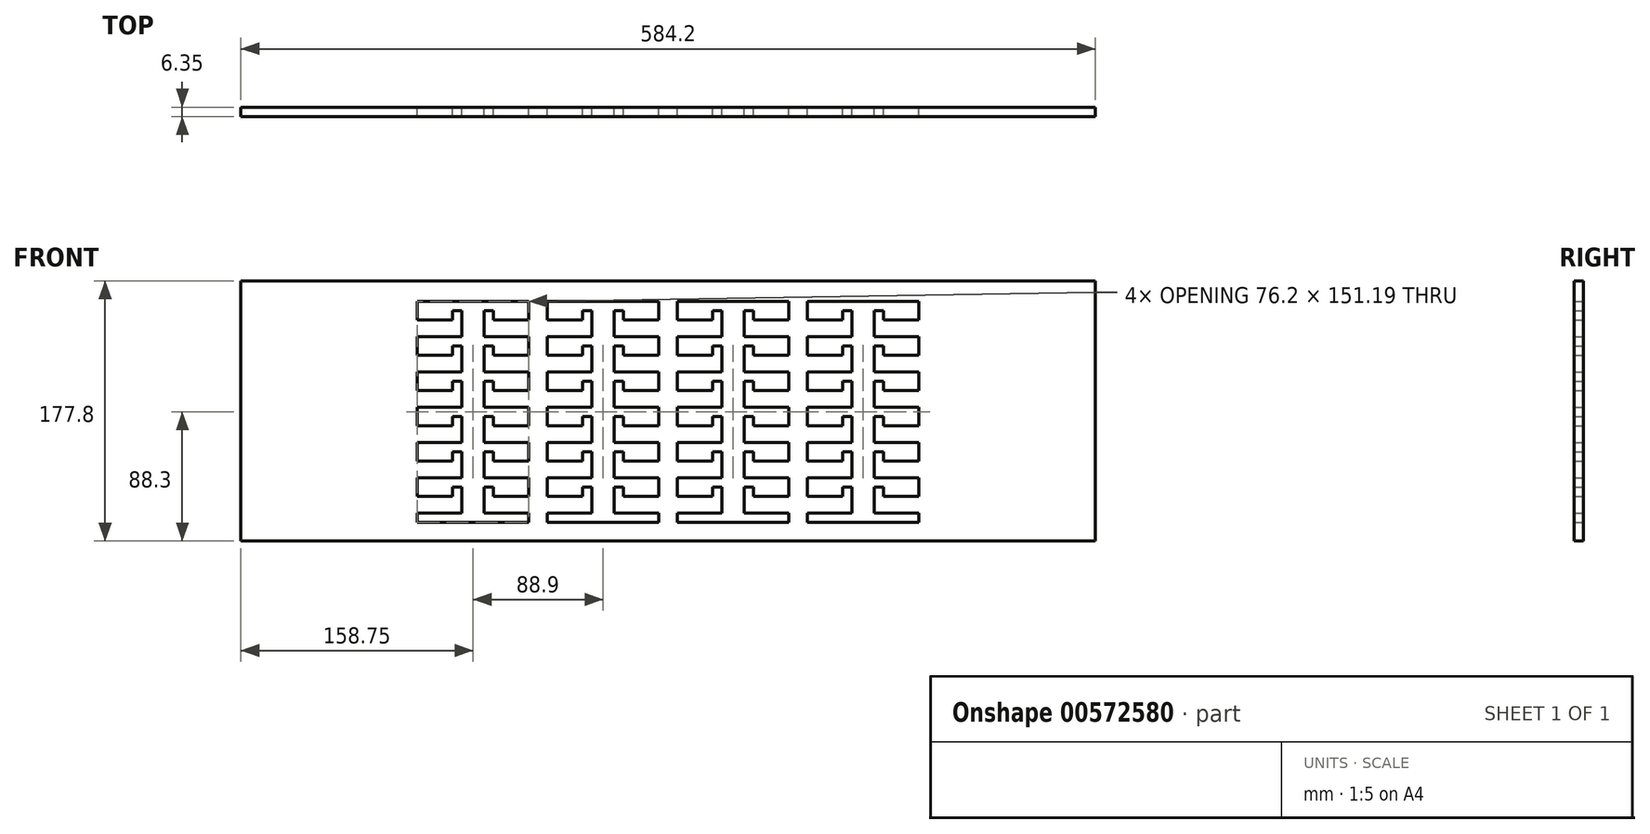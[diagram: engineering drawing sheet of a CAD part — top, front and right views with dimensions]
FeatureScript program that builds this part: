
annotation { "Feature Type Name" : "Feature", "Feature Type Description" : "" }
export const myFeature = defineFeature(function(context is Context, id is Id, definition is map)
    precondition{}
    {
        {
            var Q0;
            Q0=qCreatedBy(makeId("Front.planeOp"),FACE);
            var sketch = newSketch(context, id + "F0", { "sketchPlane" : qUnion([Q0])});
            skLineSegment(sketch, "E0", {"start": v(-97.96, -49.5) * mm, "end": v(-67.48, -49.5) * mm});
            skLineSegment(sketch, "E1", {"start": v(-67.48, -49.5) * mm, "end": v(-67.48, -31.72) * mm});
            skLineSegment(sketch, "E2", {"start": v(-67.48, -31.72) * mm, "end": v(-73.83, -31.72) * mm});
            skLineSegment(sketch, "E3", {"start": v(-73.83, -31.72) * mm, "end": v(-73.83, -38.07) * mm});
            skLineSegment(sketch, "E4", {"start": v(-73.83, -38.07) * mm, "end": v(-97.96, -38.07) * mm});
            skLineSegment(sketch, "E5", {"start": v(-97.96, -38.07) * mm, "end": v(-97.96, -25.37) * mm});
            skLineSegment(sketch, "E6", {"start": v(-97.96, -25.37) * mm, "end": v(-67.48, -25.37) * mm});
            skLineSegment(sketch, "E7", {"start": v(-67.48, -25.37) * mm, "end": v(-67.48, -7.6) * mm});
            skLineSegment(sketch, "E8", {"start": v(-67.48, -7.6) * mm, "end": v(-73.83, -7.6) * mm});
            skLineSegment(sketch, "E9", {"start": v(-73.83, -7.6) * mm, "end": v(-73.83, -13.94) * mm});
            skLineSegment(sketch, "E10", {"start": v(-73.83, -13.94) * mm, "end": v(-97.96, -13.94) * mm});
            skLineSegment(sketch, "E11", {"start": v(-97.96, -13.94) * mm, "end": v(-97.96, -1.24) * mm});
            skLineSegment(sketch, "E12", {"start": v(-97.96, -1.24) * mm, "end": v(-67.48, -1.24) * mm});
            skLineSegment(sketch, "E13", {"start": v(-67.48, -1.24) * mm, "end": v(-67.48, 16.54) * mm});
            skLineSegment(sketch, "E14", {"start": v(-67.48, 16.54) * mm, "end": v(-73.83, 16.54) * mm});
            skLineSegment(sketch, "E15", {"start": v(-73.83, 16.54) * mm, "end": v(-73.83, 10.19) * mm});
            skLineSegment(sketch, "E16", {"start": v(-73.83, 10.19) * mm, "end": v(-97.96, 10.19) * mm});
            skLineSegment(sketch, "E17", {"start": v(-97.96, 10.19) * mm, "end": v(-97.96, 22.89) * mm});
            skLineSegment(sketch, "E18", {"start": v(-97.96, 22.89) * mm, "end": v(-67.48, 22.89) * mm});
            skLineSegment(sketch, "E19", {"start": v(-67.48, 22.89) * mm, "end": v(-67.48, 40.67) * mm});
            skLineSegment(sketch, "E20", {"start": v(-67.48, 40.67) * mm, "end": v(-73.83, 40.67) * mm});
            skLineSegment(sketch, "E21", {"start": v(-73.83, 40.67) * mm, "end": v(-73.83, 34.32) * mm});
            skLineSegment(sketch, "E22", {"start": v(-73.83, 34.32) * mm, "end": v(-97.96, 34.32) * mm});
            skLineSegment(sketch, "E23", {"start": v(-97.96, 34.32) * mm, "end": v(-97.96, 47.02) * mm});
            skLineSegment(sketch, "E24", {"start": v(-97.96, 47.02) * mm, "end": v(-67.48, 47.02) * mm});
            skLineSegment(sketch, "E25", {"start": v(-67.48, 64.8) * mm, "end": v(-73.83, 64.8) * mm});
            skLineSegment(sketch, "E26", {"start": v(-73.83, 64.8) * mm, "end": v(-73.83, 58.45) * mm});
            skLineSegment(sketch, "E27", {"start": v(-73.83, 58.45) * mm, "end": v(-97.96, 58.45) * mm});
            skLineSegment(sketch, "E28", {"start": v(-97.96, 58.45) * mm, "end": v(-97.96, 71.15) * mm});
            skLineSegment(sketch, "E29", {"start": v(-21.76, -80.05) * mm, "end": v(-21.76, -73.63) * mm});
            skLineSegment(sketch, "E30", {"start": v(-21.76, -73.63) * mm, "end": v(-52.24, -73.63) * mm});
            skLineSegment(sketch, "E31", {"start": v(-52.24, -73.63) * mm, "end": v(-52.24, -55.85) * mm});
            skLineSegment(sketch, "E32", {"start": v(-52.24, -55.85) * mm, "end": v(-45.89, -55.85) * mm});
            skLineSegment(sketch, "E33", {"start": v(-45.89, -55.85) * mm, "end": v(-45.89, -62.2) * mm});
            skLineSegment(sketch, "E34", {"start": v(-45.89, -62.2) * mm, "end": v(-21.76, -62.2) * mm});
            skLineSegment(sketch, "E35", {"start": v(-21.76, -62.2) * mm, "end": v(-21.76, -49.5) * mm});
            skLineSegment(sketch, "E36", {"start": v(-21.76, -49.5) * mm, "end": v(-52.24, -49.5) * mm});
            skLineSegment(sketch, "E37", {"start": v(-52.24, -49.5) * mm, "end": v(-52.24, -31.72) * mm});
            skLineSegment(sketch, "E38", {"start": v(-52.24, -31.72) * mm, "end": v(-45.89, -31.72) * mm});
            skLineSegment(sketch, "E39", {"start": v(-45.89, -31.72) * mm, "end": v(-45.89, -38.07) * mm});
            skLineSegment(sketch, "E40", {"start": v(-45.89, -38.07) * mm, "end": v(-21.76, -38.07) * mm});
            skLineSegment(sketch, "E41", {"start": v(-21.76, -38.07) * mm, "end": v(-21.76, -25.37) * mm});
            skLineSegment(sketch, "E42", {"start": v(-21.76, -25.37) * mm, "end": v(-52.24, -25.37) * mm});
            skLineSegment(sketch, "E43", {"start": v(-52.24, -25.37) * mm, "end": v(-52.24, -7.6) * mm});
            skLineSegment(sketch, "E44", {"start": v(-52.24, -7.6) * mm, "end": v(-45.89, -7.6) * mm});
            skLineSegment(sketch, "E45", {"start": v(-45.89, -7.6) * mm, "end": v(-45.89, -13.94) * mm});
            skLineSegment(sketch, "E46", {"start": v(-45.89, -13.94) * mm, "end": v(-21.76, -13.94) * mm});
            skLineSegment(sketch, "E47", {"start": v(-21.76, -13.94) * mm, "end": v(-21.76, -1.24) * mm});
            skLineSegment(sketch, "E48", {"start": v(-21.76, -1.24) * mm, "end": v(-52.24, -1.24) * mm});
            skLineSegment(sketch, "E49", {"start": v(-52.24, -1.24) * mm, "end": v(-52.24, 16.54) * mm});
            skLineSegment(sketch, "E50", {"start": v(-52.24, 16.54) * mm, "end": v(-45.89, 16.54) * mm});
            skLineSegment(sketch, "E51", {"start": v(-45.89, 16.54) * mm, "end": v(-45.89, 10.19) * mm});
            skLineSegment(sketch, "E52", {"start": v(-45.89, 10.19) * mm, "end": v(-21.76, 10.19) * mm});
            skLineSegment(sketch, "E53", {"start": v(-21.76, 10.19) * mm, "end": v(-21.76, 22.89) * mm});
            skLineSegment(sketch, "E54", {"start": v(-21.76, 22.89) * mm, "end": v(-52.24, 22.89) * mm});
            skLineSegment(sketch, "E55", {"start": v(-52.24, 22.89) * mm, "end": v(-52.24, 40.67) * mm});
            skLineSegment(sketch, "E56", {"start": v(-52.24, 40.67) * mm, "end": v(-45.89, 40.67) * mm});
            skLineSegment(sketch, "E57", {"start": v(-45.89, 40.67) * mm, "end": v(-45.89, 34.32) * mm});
            skLineSegment(sketch, "E58", {"start": v(-45.89, 34.32) * mm, "end": v(-21.76, 34.32) * mm});
            skLineSegment(sketch, "E59", {"start": v(-21.76, 34.32) * mm, "end": v(-21.76, 47.02) * mm});
            skLineSegment(sketch, "E60", {"start": v(-21.76, 47.02) * mm, "end": v(-52.24, 47.02) * mm});
            skLineSegment(sketch, "E61", {"start": v(-52.24, 47.02) * mm, "end": v(-52.24, 64.8) * mm});
            skLineSegment(sketch, "E62", {"start": v(-52.24, 64.8) * mm, "end": v(-45.89, 64.8) * mm});
            skLineSegment(sketch, "E63", {"start": v(-45.89, 64.8) * mm, "end": v(-45.89, 58.45) * mm});
            skLineSegment(sketch, "E64", {"start": v(-45.89, 58.45) * mm, "end": v(-21.76, 58.45) * mm});
            skLineSegment(sketch, "E65", {"start": v(-21.76, 58.45) * mm, "end": v(-21.76, 71.15) * mm});
            skLineSegment(sketch, "E66", {"start": v(-67.48, 47.02) * mm, "end": v(-67.48, 64.8) * mm});
            skLineSegment(sketch, "E67", {"start": v(-67.48, -73.63) * mm, "end": v(-67.48, -55.85) * mm});
            skLineSegment(sketch, "E68", {"start": v(-73.83, -62.2) * mm, "end": v(-73.83, -55.85) * mm});
            skLineSegment(sketch, "E69", {"start": v(-73.83, -55.85) * mm, "end": v(-67.48, -55.85) * mm});
            skLineSegment(sketch, "E70", {"start": v(-67.48, -73.63) * mm, "end": v(-97.96, -73.63) * mm});
            skLineSegment(sketch, "E71", {"start": v(-97.96, -62.2) * mm, "end": v(-97.96, -49.5) * mm});
            skLineSegment(sketch, "E72", {"start": v(-97.96, -73.63) * mm, "end": v(-97.96, -80.05) * mm});
            skLineSegment(sketch, "E73", {"start": v(-97.96, -62.2) * mm, "end": v(-73.83, -62.2) * mm});
            skLineSegment(sketch, "E74", {"start": v(-97.96, -80.05) * mm, "end": v(-21.76, -80.05) * mm});
            skLineSegment(sketch, "E75", {"start": v(-97.96, 71.15) * mm, "end": v(-21.76, 71.15) * mm});
            skPoint(sketch, "E76", {"position": v(-59.86, 71.15) * mm});
            skPoint(sketch, "E77", {"position": v(-59.86, -80.05) * mm});
            skLineSegment(sketch, "E78", {"start": v(-186.86, -49.5) * mm, "end": v(-156.38, -49.5) * mm});
            skLineSegment(sketch, "E79", {"start": v(-156.38, -49.5) * mm, "end": v(-156.38, -31.72) * mm});
            skLineSegment(sketch, "E80", {"start": v(-156.38, -31.72) * mm, "end": v(-162.73, -31.72) * mm});
            skLineSegment(sketch, "E81", {"start": v(-162.73, -31.72) * mm, "end": v(-162.73, -38.07) * mm});
            skLineSegment(sketch, "E82", {"start": v(-162.73, -38.07) * mm, "end": v(-186.86, -38.07) * mm});
            skLineSegment(sketch, "E83", {"start": v(-186.86, -38.07) * mm, "end": v(-186.86, -25.37) * mm});
            skLineSegment(sketch, "E84", {"start": v(-186.86, -25.37) * mm, "end": v(-156.38, -25.37) * mm});
            skLineSegment(sketch, "E85", {"start": v(-156.38, -25.37) * mm, "end": v(-156.38, -7.6) * mm});
            skLineSegment(sketch, "E86", {"start": v(-156.38, -7.6) * mm, "end": v(-162.73, -7.6) * mm});
            skLineSegment(sketch, "E87", {"start": v(-162.73, -7.6) * mm, "end": v(-162.73, -13.94) * mm});
            skLineSegment(sketch, "E88", {"start": v(-162.73, -13.94) * mm, "end": v(-186.86, -13.94) * mm});
            skLineSegment(sketch, "E89", {"start": v(-186.86, -13.94) * mm, "end": v(-186.86, -1.24) * mm});
            skLineSegment(sketch, "E90", {"start": v(-186.86, -1.24) * mm, "end": v(-156.38, -1.24) * mm});
            skLineSegment(sketch, "E91", {"start": v(-156.38, -1.24) * mm, "end": v(-156.38, 16.54) * mm});
            skLineSegment(sketch, "E92", {"start": v(-156.38, 16.54) * mm, "end": v(-162.73, 16.54) * mm});
            skLineSegment(sketch, "E93", {"start": v(-162.73, 16.54) * mm, "end": v(-162.73, 10.19) * mm});
            skLineSegment(sketch, "E94", {"start": v(-162.73, 10.19) * mm, "end": v(-186.86, 10.19) * mm});
            skLineSegment(sketch, "E95", {"start": v(-186.86, 10.19) * mm, "end": v(-186.86, 22.89) * mm});
            skLineSegment(sketch, "E96", {"start": v(-186.86, 22.89) * mm, "end": v(-156.38, 22.89) * mm});
            skLineSegment(sketch, "E97", {"start": v(-156.38, 22.89) * mm, "end": v(-156.38, 40.67) * mm});
            skLineSegment(sketch, "E98", {"start": v(-156.38, 40.67) * mm, "end": v(-162.73, 40.67) * mm});
            skLineSegment(sketch, "E99", {"start": v(-162.73, 40.67) * mm, "end": v(-162.73, 34.32) * mm});
            skLineSegment(sketch, "E100", {"start": v(-162.73, 34.32) * mm, "end": v(-186.86, 34.32) * mm});
            skLineSegment(sketch, "E101", {"start": v(-186.86, 34.32) * mm, "end": v(-186.86, 47.02) * mm});
            skLineSegment(sketch, "E102", {"start": v(-186.86, 47.02) * mm, "end": v(-156.38, 47.02) * mm});
            skLineSegment(sketch, "E103", {"start": v(-156.38, 64.8) * mm, "end": v(-162.73, 64.8) * mm});
            skLineSegment(sketch, "E104", {"start": v(-162.73, 64.8) * mm, "end": v(-162.73, 58.45) * mm});
            skLineSegment(sketch, "E105", {"start": v(-162.73, 58.45) * mm, "end": v(-186.86, 58.45) * mm});
            skLineSegment(sketch, "E106", {"start": v(-186.86, 58.45) * mm, "end": v(-186.86, 71.15) * mm});
            skLineSegment(sketch, "E107", {"start": v(-110.66, -80.05) * mm, "end": v(-110.66, -73.63) * mm});
            skLineSegment(sketch, "E108", {"start": v(-110.66, -73.63) * mm, "end": v(-141.14, -73.63) * mm});
            skLineSegment(sketch, "E109", {"start": v(-141.14, -73.63) * mm, "end": v(-141.14, -55.85) * mm});
            skLineSegment(sketch, "E110", {"start": v(-141.14, -55.85) * mm, "end": v(-134.79, -55.85) * mm});
            skLineSegment(sketch, "E111", {"start": v(-134.79, -55.85) * mm, "end": v(-134.79, -62.2) * mm});
            skLineSegment(sketch, "E112", {"start": v(-134.79, -62.2) * mm, "end": v(-110.66, -62.2) * mm});
            skLineSegment(sketch, "E113", {"start": v(-110.66, -62.2) * mm, "end": v(-110.66, -49.5) * mm});
            skLineSegment(sketch, "E114", {"start": v(-110.66, -49.5) * mm, "end": v(-141.14, -49.5) * mm});
            skLineSegment(sketch, "E115", {"start": v(-141.14, -49.5) * mm, "end": v(-141.14, -31.72) * mm});
            skLineSegment(sketch, "E116", {"start": v(-141.14, -31.72) * mm, "end": v(-134.79, -31.72) * mm});
            skLineSegment(sketch, "E117", {"start": v(-134.79, -31.72) * mm, "end": v(-134.79, -38.07) * mm});
            skLineSegment(sketch, "E118", {"start": v(-134.79, -38.07) * mm, "end": v(-110.66, -38.07) * mm});
            skLineSegment(sketch, "E119", {"start": v(-110.66, -38.07) * mm, "end": v(-110.66, -25.37) * mm});
            skLineSegment(sketch, "E120", {"start": v(-110.66, -25.37) * mm, "end": v(-141.14, -25.37) * mm});
            skLineSegment(sketch, "E121", {"start": v(-141.14, -25.37) * mm, "end": v(-141.14, -7.6) * mm});
            skLineSegment(sketch, "E122", {"start": v(-141.14, -7.6) * mm, "end": v(-134.79, -7.6) * mm});
            skLineSegment(sketch, "E123", {"start": v(-134.79, -7.6) * mm, "end": v(-134.79, -13.94) * mm});
            skLineSegment(sketch, "E124", {"start": v(-134.79, -13.94) * mm, "end": v(-110.66, -13.94) * mm});
            skLineSegment(sketch, "E125", {"start": v(-110.66, -13.94) * mm, "end": v(-110.66, -1.24) * mm});
            skLineSegment(sketch, "E126", {"start": v(-110.66, -1.24) * mm, "end": v(-141.14, -1.24) * mm});
            skLineSegment(sketch, "E127", {"start": v(-141.14, -1.24) * mm, "end": v(-141.14, 16.54) * mm});
            skLineSegment(sketch, "E128", {"start": v(-141.14, 16.54) * mm, "end": v(-134.79, 16.54) * mm});
            skLineSegment(sketch, "E129", {"start": v(-134.79, 16.54) * mm, "end": v(-134.79, 10.19) * mm});
            skLineSegment(sketch, "E130", {"start": v(-134.79, 10.19) * mm, "end": v(-110.66, 10.19) * mm});
            skLineSegment(sketch, "E131", {"start": v(-110.66, 10.19) * mm, "end": v(-110.66, 22.89) * mm});
            skLineSegment(sketch, "E132", {"start": v(-110.66, 22.89) * mm, "end": v(-141.14, 22.89) * mm});
            skLineSegment(sketch, "E133", {"start": v(-141.14, 22.89) * mm, "end": v(-141.14, 40.67) * mm});
            skLineSegment(sketch, "E134", {"start": v(-141.14, 40.67) * mm, "end": v(-134.79, 40.67) * mm});
            skLineSegment(sketch, "E135", {"start": v(-134.79, 40.67) * mm, "end": v(-134.79, 34.32) * mm});
            skLineSegment(sketch, "E136", {"start": v(-134.79, 34.32) * mm, "end": v(-110.66, 34.32) * mm});
            skLineSegment(sketch, "E137", {"start": v(-110.66, 34.32) * mm, "end": v(-110.66, 47.02) * mm});
            skLineSegment(sketch, "E138", {"start": v(-110.66, 47.02) * mm, "end": v(-141.14, 47.02) * mm});
            skLineSegment(sketch, "E139", {"start": v(-141.14, 47.02) * mm, "end": v(-141.14, 64.8) * mm});
            skLineSegment(sketch, "E140", {"start": v(-141.14, 64.8) * mm, "end": v(-134.79, 64.8) * mm});
            skLineSegment(sketch, "E141", {"start": v(-134.79, 64.8) * mm, "end": v(-134.79, 58.45) * mm});
            skLineSegment(sketch, "E142", {"start": v(-134.79, 58.45) * mm, "end": v(-110.66, 58.45) * mm});
            skLineSegment(sketch, "E143", {"start": v(-110.66, 58.45) * mm, "end": v(-110.66, 71.15) * mm});
            skLineSegment(sketch, "E144", {"start": v(-156.38, 47.02) * mm, "end": v(-156.38, 64.8) * mm});
            skLineSegment(sketch, "E145", {"start": v(-156.38, -73.63) * mm, "end": v(-156.38, -55.85) * mm});
            skLineSegment(sketch, "E146", {"start": v(-162.73, -62.2) * mm, "end": v(-162.73, -55.85) * mm});
            skLineSegment(sketch, "E147", {"start": v(-162.73, -55.85) * mm, "end": v(-156.38, -55.85) * mm});
            skLineSegment(sketch, "E148", {"start": v(-156.38, -73.63) * mm, "end": v(-186.86, -73.63) * mm});
            skLineSegment(sketch, "E149", {"start": v(-186.86, -62.2) * mm, "end": v(-186.86, -49.5) * mm});
            skLineSegment(sketch, "E150", {"start": v(-186.86, -73.63) * mm, "end": v(-186.86, -80.05) * mm});
            skLineSegment(sketch, "E151", {"start": v(-186.86, -62.2) * mm, "end": v(-162.73, -62.2) * mm});
            skLineSegment(sketch, "E152", {"start": v(-186.86, -80.05) * mm, "end": v(-110.66, -80.05) * mm});
            skLineSegment(sketch, "E153", {"start": v(-186.86, 71.15) * mm, "end": v(-110.66, 71.15) * mm});
            skPoint(sketch, "E154", {"position": v(-148.76, 71.15) * mm});
            skPoint(sketch, "E155", {"position": v(-148.76, -80.05) * mm});
            skLineSegment(sketch, "E156", {"start": v(-275.76, -49.5) * mm, "end": v(-245.28, -49.5) * mm});
            skLineSegment(sketch, "E157", {"start": v(-245.28, -49.5) * mm, "end": v(-245.28, -31.72) * mm});
            skLineSegment(sketch, "E158", {"start": v(-245.28, -31.72) * mm, "end": v(-251.63, -31.72) * mm});
            skLineSegment(sketch, "E159", {"start": v(-251.63, -31.72) * mm, "end": v(-251.63, -38.07) * mm});
            skLineSegment(sketch, "E160", {"start": v(-251.63, -38.07) * mm, "end": v(-275.76, -38.07) * mm});
            skLineSegment(sketch, "E161", {"start": v(-275.76, -38.07) * mm, "end": v(-275.76, -25.37) * mm});
            skLineSegment(sketch, "E162", {"start": v(-275.76, -25.37) * mm, "end": v(-245.28, -25.37) * mm});
            skLineSegment(sketch, "E163", {"start": v(-245.28, -25.37) * mm, "end": v(-245.28, -7.6) * mm});
            skLineSegment(sketch, "E164", {"start": v(-245.28, -7.6) * mm, "end": v(-251.63, -7.6) * mm});
            skLineSegment(sketch, "E165", {"start": v(-251.63, -7.6) * mm, "end": v(-251.63, -13.94) * mm});
            skLineSegment(sketch, "E166", {"start": v(-251.63, -13.94) * mm, "end": v(-275.76, -13.94) * mm});
            skLineSegment(sketch, "E167", {"start": v(-275.76, -13.94) * mm, "end": v(-275.76, -1.24) * mm});
            skLineSegment(sketch, "E168", {"start": v(-275.76, -1.24) * mm, "end": v(-245.28, -1.24) * mm});
            skLineSegment(sketch, "E169", {"start": v(-245.28, -1.24) * mm, "end": v(-245.28, 16.54) * mm});
            skLineSegment(sketch, "E170", {"start": v(-245.28, 16.54) * mm, "end": v(-251.63, 16.54) * mm});
            skLineSegment(sketch, "E171", {"start": v(-251.63, 16.54) * mm, "end": v(-251.63, 10.19) * mm});
            skLineSegment(sketch, "E172", {"start": v(-251.63, 10.19) * mm, "end": v(-275.76, 10.19) * mm});
            skLineSegment(sketch, "E173", {"start": v(-275.76, 10.19) * mm, "end": v(-275.76, 22.89) * mm});
            skLineSegment(sketch, "E174", {"start": v(-275.76, 22.89) * mm, "end": v(-245.28, 22.89) * mm});
            skLineSegment(sketch, "E175", {"start": v(-245.28, 22.89) * mm, "end": v(-245.28, 40.67) * mm});
            skLineSegment(sketch, "E176", {"start": v(-245.28, 40.67) * mm, "end": v(-251.63, 40.67) * mm});
            skLineSegment(sketch, "E177", {"start": v(-251.63, 40.67) * mm, "end": v(-251.63, 34.32) * mm});
            skLineSegment(sketch, "E178", {"start": v(-251.63, 34.32) * mm, "end": v(-275.76, 34.32) * mm});
            skLineSegment(sketch, "E179", {"start": v(-275.76, 34.32) * mm, "end": v(-275.76, 47.02) * mm});
            skLineSegment(sketch, "E180", {"start": v(-275.76, 47.02) * mm, "end": v(-245.28, 47.02) * mm});
            skLineSegment(sketch, "E181", {"start": v(-245.28, 64.8) * mm, "end": v(-251.63, 64.8) * mm});
            skLineSegment(sketch, "E182", {"start": v(-251.63, 64.8) * mm, "end": v(-251.63, 58.45) * mm});
            skLineSegment(sketch, "E183", {"start": v(-251.63, 58.45) * mm, "end": v(-275.76, 58.45) * mm});
            skLineSegment(sketch, "E184", {"start": v(-275.76, 58.45) * mm, "end": v(-275.76, 71.15) * mm});
            skLineSegment(sketch, "E185", {"start": v(-199.56, -80.05) * mm, "end": v(-199.56, -73.63) * mm});
            skLineSegment(sketch, "E186", {"start": v(-199.56, -73.63) * mm, "end": v(-230.04, -73.63) * mm});
            skLineSegment(sketch, "E187", {"start": v(-230.04, -73.63) * mm, "end": v(-230.04, -55.85) * mm});
            skLineSegment(sketch, "E188", {"start": v(-230.04, -55.85) * mm, "end": v(-223.69, -55.85) * mm});
            skLineSegment(sketch, "E189", {"start": v(-223.69, -55.85) * mm, "end": v(-223.69, -62.2) * mm});
            skLineSegment(sketch, "E190", {"start": v(-223.69, -62.2) * mm, "end": v(-199.56, -62.2) * mm});
            skLineSegment(sketch, "E191", {"start": v(-199.56, -62.2) * mm, "end": v(-199.56, -49.5) * mm});
            skLineSegment(sketch, "E192", {"start": v(-199.56, -49.5) * mm, "end": v(-230.04, -49.5) * mm});
            skLineSegment(sketch, "E193", {"start": v(-230.04, -49.5) * mm, "end": v(-230.04, -31.72) * mm});
            skLineSegment(sketch, "E194", {"start": v(-230.04, -31.72) * mm, "end": v(-223.69, -31.72) * mm});
            skLineSegment(sketch, "E195", {"start": v(-223.69, -31.72) * mm, "end": v(-223.69, -38.07) * mm});
            skLineSegment(sketch, "E196", {"start": v(-223.69, -38.07) * mm, "end": v(-199.56, -38.07) * mm});
            skLineSegment(sketch, "E197", {"start": v(-199.56, -38.07) * mm, "end": v(-199.56, -25.37) * mm});
            skLineSegment(sketch, "E198", {"start": v(-199.56, -25.37) * mm, "end": v(-230.04, -25.37) * mm});
            skLineSegment(sketch, "E199", {"start": v(-230.04, -25.37) * mm, "end": v(-230.04, -7.6) * mm});
            skLineSegment(sketch, "E200", {"start": v(-230.04, -7.6) * mm, "end": v(-223.69, -7.6) * mm});
            skLineSegment(sketch, "E201", {"start": v(-223.69, -7.6) * mm, "end": v(-223.69, -13.94) * mm});
            skLineSegment(sketch, "E202", {"start": v(-223.69, -13.94) * mm, "end": v(-199.56, -13.94) * mm});
            skLineSegment(sketch, "E203", {"start": v(-199.56, -13.94) * mm, "end": v(-199.56, -1.24) * mm});
            skLineSegment(sketch, "E204", {"start": v(-199.56, -1.24) * mm, "end": v(-230.04, -1.24) * mm});
            skLineSegment(sketch, "E205", {"start": v(-230.04, -1.24) * mm, "end": v(-230.04, 16.54) * mm});
            skLineSegment(sketch, "E206", {"start": v(-230.04, 16.54) * mm, "end": v(-223.69, 16.54) * mm});
            skLineSegment(sketch, "E207", {"start": v(-223.69, 16.54) * mm, "end": v(-223.69, 10.19) * mm});
            skLineSegment(sketch, "E208", {"start": v(-223.69, 10.19) * mm, "end": v(-199.56, 10.19) * mm});
            skLineSegment(sketch, "E209", {"start": v(-199.56, 10.19) * mm, "end": v(-199.56, 22.89) * mm});
            skLineSegment(sketch, "E210", {"start": v(-199.56, 22.89) * mm, "end": v(-230.04, 22.89) * mm});
            skLineSegment(sketch, "E211", {"start": v(-230.04, 22.89) * mm, "end": v(-230.04, 40.67) * mm});
            skLineSegment(sketch, "E212", {"start": v(-230.04, 40.67) * mm, "end": v(-223.69, 40.67) * mm});
            skLineSegment(sketch, "E213", {"start": v(-223.69, 40.67) * mm, "end": v(-223.69, 34.32) * mm});
            skLineSegment(sketch, "E214", {"start": v(-223.69, 34.32) * mm, "end": v(-199.56, 34.32) * mm});
            skLineSegment(sketch, "E215", {"start": v(-199.56, 34.32) * mm, "end": v(-199.56, 47.02) * mm});
            skLineSegment(sketch, "E216", {"start": v(-199.56, 47.02) * mm, "end": v(-230.04, 47.02) * mm});
            skLineSegment(sketch, "E217", {"start": v(-230.04, 47.02) * mm, "end": v(-230.04, 64.8) * mm});
            skLineSegment(sketch, "E218", {"start": v(-230.04, 64.8) * mm, "end": v(-223.69, 64.8) * mm});
            skLineSegment(sketch, "E219", {"start": v(-223.69, 64.8) * mm, "end": v(-223.69, 58.45) * mm});
            skLineSegment(sketch, "E220", {"start": v(-223.69, 58.45) * mm, "end": v(-199.56, 58.45) * mm});
            skLineSegment(sketch, "E221", {"start": v(-199.56, 58.45) * mm, "end": v(-199.56, 71.15) * mm});
            skLineSegment(sketch, "E222", {"start": v(-245.28, 47.02) * mm, "end": v(-245.28, 64.8) * mm});
            skLineSegment(sketch, "E223", {"start": v(-245.28, -73.63) * mm, "end": v(-245.28, -55.85) * mm});
            skLineSegment(sketch, "E224", {"start": v(-251.63, -62.2) * mm, "end": v(-251.63, -55.85) * mm});
            skLineSegment(sketch, "E225", {"start": v(-251.63, -55.85) * mm, "end": v(-245.28, -55.85) * mm});
            skLineSegment(sketch, "E226", {"start": v(-245.28, -73.63) * mm, "end": v(-275.76, -73.63) * mm});
            skLineSegment(sketch, "E227", {"start": v(-275.76, -62.2) * mm, "end": v(-275.76, -49.5) * mm});
            skLineSegment(sketch, "E228", {"start": v(-275.76, -73.63) * mm, "end": v(-275.76, -80.05) * mm});
            skLineSegment(sketch, "E229", {"start": v(-275.76, -62.2) * mm, "end": v(-251.63, -62.2) * mm});
            skLineSegment(sketch, "E230", {"start": v(-275.76, -80.05) * mm, "end": v(-199.56, -80.05) * mm});
            skLineSegment(sketch, "E231", {"start": v(-275.76, 71.15) * mm, "end": v(-199.56, 71.15) * mm});
            skPoint(sketch, "E232", {"position": v(-237.66, 71.15) * mm});
            skPoint(sketch, "E233", {"position": v(-237.66, -80.05) * mm});
            skLineSegment(sketch, "E234", {"start": v(-364.66, -49.5) * mm, "end": v(-334.18, -49.5) * mm});
            skLineSegment(sketch, "E235", {"start": v(-334.18, -49.5) * mm, "end": v(-334.18, -31.72) * mm});
            skLineSegment(sketch, "E236", {"start": v(-334.18, -31.72) * mm, "end": v(-340.53, -31.72) * mm});
            skLineSegment(sketch, "E237", {"start": v(-340.53, -31.72) * mm, "end": v(-340.53, -38.07) * mm});
            skLineSegment(sketch, "E238", {"start": v(-340.53, -38.07) * mm, "end": v(-364.66, -38.07) * mm});
            skLineSegment(sketch, "E239", {"start": v(-364.66, -38.07) * mm, "end": v(-364.66, -25.37) * mm});
            skLineSegment(sketch, "E240", {"start": v(-364.66, -25.37) * mm, "end": v(-334.18, -25.37) * mm});
            skLineSegment(sketch, "E241", {"start": v(-334.18, -25.37) * mm, "end": v(-334.18, -7.6) * mm});
            skLineSegment(sketch, "E242", {"start": v(-334.18, -7.6) * mm, "end": v(-340.53, -7.6) * mm});
            skLineSegment(sketch, "E243", {"start": v(-340.53, -7.6) * mm, "end": v(-340.53, -13.94) * mm});
            skLineSegment(sketch, "E244", {"start": v(-340.53, -13.94) * mm, "end": v(-364.66, -13.94) * mm});
            skLineSegment(sketch, "E245", {"start": v(-364.66, -13.94) * mm, "end": v(-364.66, -1.24) * mm});
            skLineSegment(sketch, "E246", {"start": v(-364.66, -1.24) * mm, "end": v(-334.18, -1.24) * mm});
            skLineSegment(sketch, "E247", {"start": v(-334.18, -1.24) * mm, "end": v(-334.18, 16.54) * mm});
            skLineSegment(sketch, "E248", {"start": v(-334.18, 16.54) * mm, "end": v(-340.53, 16.54) * mm});
            skLineSegment(sketch, "E249", {"start": v(-340.53, 16.54) * mm, "end": v(-340.53, 10.19) * mm});
            skLineSegment(sketch, "E250", {"start": v(-340.53, 10.19) * mm, "end": v(-364.66, 10.19) * mm});
            skLineSegment(sketch, "E251", {"start": v(-364.66, 10.19) * mm, "end": v(-364.66, 22.89) * mm});
            skLineSegment(sketch, "E252", {"start": v(-364.66, 22.89) * mm, "end": v(-334.18, 22.89) * mm});
            skLineSegment(sketch, "E253", {"start": v(-334.18, 22.89) * mm, "end": v(-334.18, 40.67) * mm});
            skLineSegment(sketch, "E254", {"start": v(-334.18, 40.67) * mm, "end": v(-340.53, 40.67) * mm});
            skLineSegment(sketch, "E255", {"start": v(-340.53, 40.67) * mm, "end": v(-340.53, 34.32) * mm});
            skLineSegment(sketch, "E256", {"start": v(-340.53, 34.32) * mm, "end": v(-364.66, 34.32) * mm});
            skLineSegment(sketch, "E257", {"start": v(-364.66, 34.32) * mm, "end": v(-364.66, 47.02) * mm});
            skLineSegment(sketch, "E258", {"start": v(-364.66, 47.02) * mm, "end": v(-334.18, 47.02) * mm});
            skLineSegment(sketch, "E259", {"start": v(-334.18, 64.8) * mm, "end": v(-340.53, 64.8) * mm});
            skLineSegment(sketch, "E260", {"start": v(-340.53, 64.8) * mm, "end": v(-340.53, 58.45) * mm});
            skLineSegment(sketch, "E261", {"start": v(-340.53, 58.45) * mm, "end": v(-364.66, 58.45) * mm});
            skLineSegment(sketch, "E262", {"start": v(-364.66, 58.45) * mm, "end": v(-364.66, 71.15) * mm});
            skLineSegment(sketch, "E263", {"start": v(-288.46, -80.05) * mm, "end": v(-288.46, -73.63) * mm});
            skLineSegment(sketch, "E264", {"start": v(-288.46, -73.63) * mm, "end": v(-318.94, -73.63) * mm});
            skLineSegment(sketch, "E265", {"start": v(-318.94, -73.63) * mm, "end": v(-318.94, -55.85) * mm});
            skLineSegment(sketch, "E266", {"start": v(-318.94, -55.85) * mm, "end": v(-312.59, -55.85) * mm});
            skLineSegment(sketch, "E267", {"start": v(-312.59, -55.85) * mm, "end": v(-312.59, -62.2) * mm});
            skLineSegment(sketch, "E268", {"start": v(-312.59, -62.2) * mm, "end": v(-288.46, -62.2) * mm});
            skLineSegment(sketch, "E269", {"start": v(-288.46, -62.2) * mm, "end": v(-288.46, -49.5) * mm});
            skLineSegment(sketch, "E270", {"start": v(-288.46, -49.5) * mm, "end": v(-318.94, -49.5) * mm});
            skLineSegment(sketch, "E271", {"start": v(-318.94, -49.5) * mm, "end": v(-318.94, -31.72) * mm});
            skLineSegment(sketch, "E272", {"start": v(-318.94, -31.72) * mm, "end": v(-312.59, -31.72) * mm});
            skLineSegment(sketch, "E273", {"start": v(-312.59, -31.72) * mm, "end": v(-312.59, -38.07) * mm});
            skLineSegment(sketch, "E274", {"start": v(-312.59, -38.07) * mm, "end": v(-288.46, -38.07) * mm});
            skLineSegment(sketch, "E275", {"start": v(-288.46, -38.07) * mm, "end": v(-288.46, -25.37) * mm});
            skLineSegment(sketch, "E276", {"start": v(-288.46, -25.37) * mm, "end": v(-318.94, -25.37) * mm});
            skLineSegment(sketch, "E277", {"start": v(-318.94, -25.37) * mm, "end": v(-318.94, -7.6) * mm});
            skLineSegment(sketch, "E278", {"start": v(-318.94, -7.6) * mm, "end": v(-312.59, -7.6) * mm});
            skLineSegment(sketch, "E279", {"start": v(-312.59, -7.6) * mm, "end": v(-312.59, -13.94) * mm});
            skLineSegment(sketch, "E280", {"start": v(-312.59, -13.94) * mm, "end": v(-288.46, -13.94) * mm});
            skLineSegment(sketch, "E281", {"start": v(-288.46, -13.94) * mm, "end": v(-288.46, -1.24) * mm});
            skLineSegment(sketch, "E282", {"start": v(-288.46, -1.24) * mm, "end": v(-318.94, -1.24) * mm});
            skLineSegment(sketch, "E283", {"start": v(-318.94, -1.24) * mm, "end": v(-318.94, 16.54) * mm});
            skLineSegment(sketch, "E284", {"start": v(-318.94, 16.54) * mm, "end": v(-312.59, 16.54) * mm});
            skLineSegment(sketch, "E285", {"start": v(-312.59, 16.54) * mm, "end": v(-312.59, 10.19) * mm});
            skLineSegment(sketch, "E286", {"start": v(-312.59, 10.19) * mm, "end": v(-288.46, 10.19) * mm});
            skLineSegment(sketch, "E287", {"start": v(-288.46, 10.19) * mm, "end": v(-288.46, 22.89) * mm});
            skLineSegment(sketch, "E288", {"start": v(-288.46, 22.89) * mm, "end": v(-318.94, 22.89) * mm});
            skLineSegment(sketch, "E289", {"start": v(-318.94, 22.89) * mm, "end": v(-318.94, 40.67) * mm});
            skLineSegment(sketch, "E290", {"start": v(-318.94, 40.67) * mm, "end": v(-312.59, 40.67) * mm});
            skLineSegment(sketch, "E291", {"start": v(-312.59, 40.67) * mm, "end": v(-312.59, 34.32) * mm});
            skLineSegment(sketch, "E292", {"start": v(-312.59, 34.32) * mm, "end": v(-288.46, 34.32) * mm});
            skLineSegment(sketch, "E293", {"start": v(-288.46, 34.32) * mm, "end": v(-288.46, 47.02) * mm});
            skLineSegment(sketch, "E294", {"start": v(-288.46, 47.02) * mm, "end": v(-318.94, 47.02) * mm});
            skLineSegment(sketch, "E295", {"start": v(-318.94, 47.02) * mm, "end": v(-318.94, 64.8) * mm});
            skLineSegment(sketch, "E296", {"start": v(-318.94, 64.8) * mm, "end": v(-312.59, 64.8) * mm});
            skLineSegment(sketch, "E297", {"start": v(-312.59, 64.8) * mm, "end": v(-312.59, 58.45) * mm});
            skLineSegment(sketch, "E298", {"start": v(-312.59, 58.45) * mm, "end": v(-288.46, 58.45) * mm});
            skLineSegment(sketch, "E299", {"start": v(-288.46, 58.45) * mm, "end": v(-288.46, 71.15) * mm});
            skLineSegment(sketch, "E300", {"start": v(-334.18, 47.02) * mm, "end": v(-334.18, 64.8) * mm});
            skLineSegment(sketch, "E301", {"start": v(-334.18, -73.63) * mm, "end": v(-334.18, -55.85) * mm});
            skLineSegment(sketch, "E302", {"start": v(-340.53, -62.2) * mm, "end": v(-340.53, -55.85) * mm});
            skLineSegment(sketch, "E303", {"start": v(-340.53, -55.85) * mm, "end": v(-334.18, -55.85) * mm});
            skLineSegment(sketch, "E304", {"start": v(-334.18, -73.63) * mm, "end": v(-364.66, -73.63) * mm});
            skLineSegment(sketch, "E305", {"start": v(-364.66, -62.2) * mm, "end": v(-364.66, -49.5) * mm});
            skLineSegment(sketch, "E306", {"start": v(-364.66, -73.63) * mm, "end": v(-364.66, -80.05) * mm});
            skLineSegment(sketch, "E307", {"start": v(-364.66, -62.2) * mm, "end": v(-340.53, -62.2) * mm});
            skLineSegment(sketch, "E308", {"start": v(-364.66, -80.05) * mm, "end": v(-288.46, -80.05) * mm});
            skLineSegment(sketch, "E309", {"start": v(-364.66, 71.15) * mm, "end": v(-288.46, 71.15) * mm});
            skPoint(sketch, "E310", {"position": v(-326.56, 71.15) * mm});
            skPoint(sketch, "E311", {"position": v(-326.56, -80.05) * mm});
            skLineSegment(sketch, "E312.bottom", {"start": v(98.9, 85.05) * mm, "end": v(-485.3, 85.05) * mm});
            skLineSegment(sketch, "E312.top", {"start": v(98.9, -92.75) * mm, "end": v(-485.3, -92.75) * mm});
            skLineSegment(sketch, "E312.left", {"start": v(98.9, 85.05) * mm, "end": v(98.9, -92.75) * mm});
            skLineSegment(sketch, "E312.right", {"start": v(-485.3, 85.05) * mm, "end": v(-485.3, -92.75) * mm});
            skPoint(sketch, "E313", {"position": v(-193.2, 85.05) * mm});
            skLineSegment(sketch, "E314", {"start": v(-199.56, 71.15) * mm, "end": v(-186.86, 71.15) * mm});
            skPoint(sketch, "E315", {"position": v(-193.2, 71.15) * mm});
            skSolve(sketch);
        }
        {
            var Q0;
            Q0=makeQuery(id+"F0.imprint","IMPRINT",FACE,{"disambiguationData":[TD([[makeQuery(id+"F0.imprint","IMPRINT",EDGE,{"derivedFrom":sQuery(id+"F0.wireOp",EDGE,"E0")}),1.0]])]});
            extrude(context, id + "F1", {"entities" : qUnion([Q0]), "depth" : 6.35 * mm});
        }
    });
